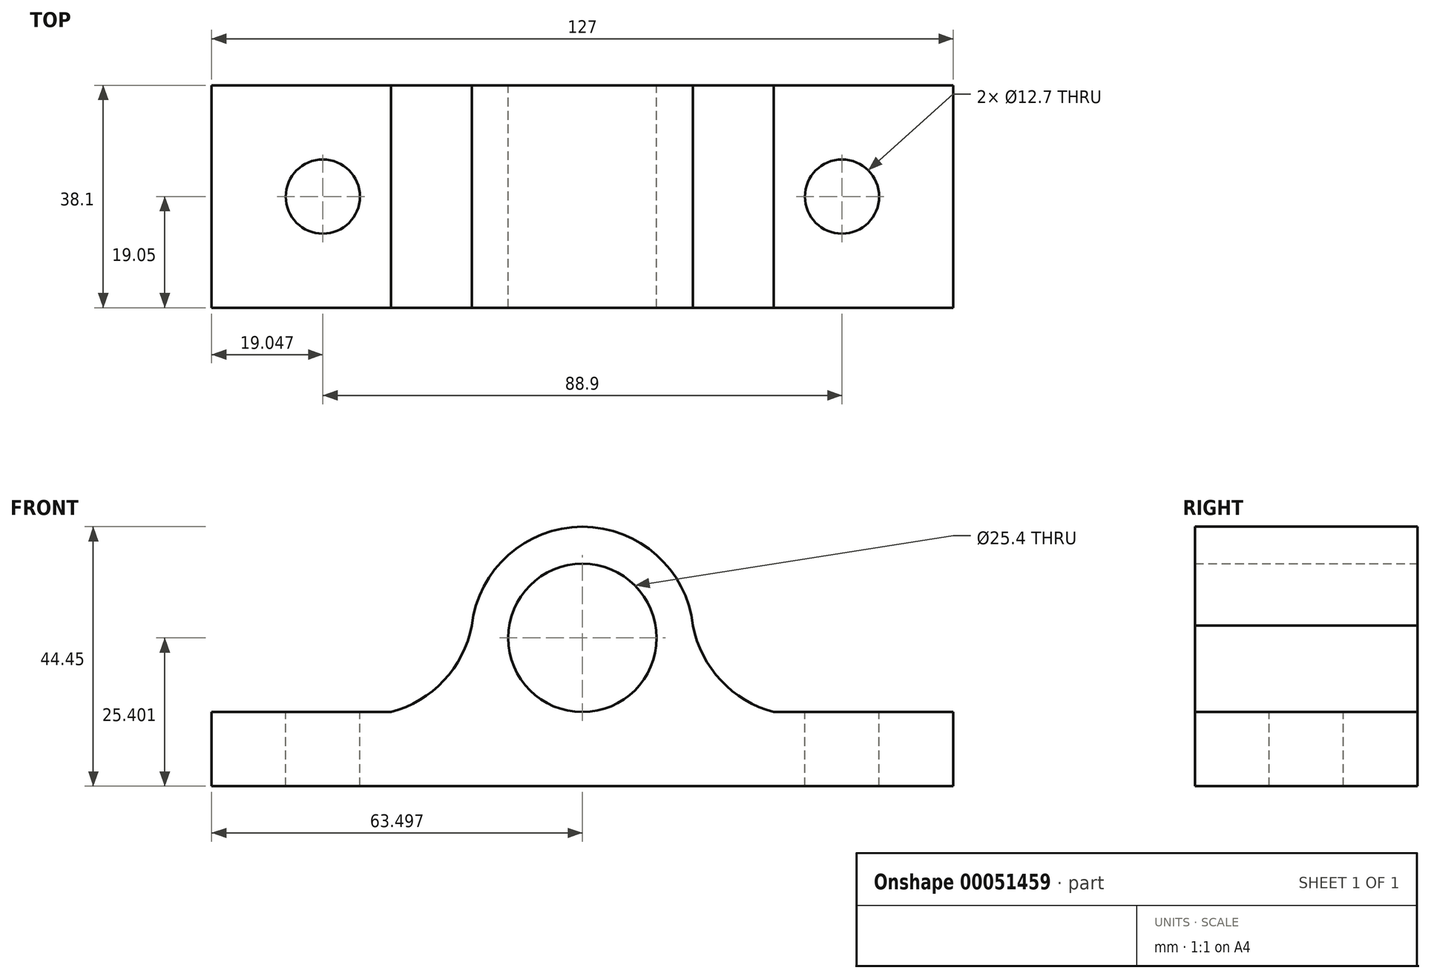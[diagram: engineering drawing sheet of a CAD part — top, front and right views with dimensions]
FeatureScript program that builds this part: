
annotation { "Feature Type Name" : "Feature", "Feature Type Description" : "" }
export const myFeature = defineFeature(function(context is Context, id is Id, definition is map)
    precondition{}
    {
        {
            var Q0;
            Q0=qCreatedBy(makeId("Front.planeOp"),FACE);
            var sketch = newSketch(context, id + "F0", { "sketchPlane" : qUnion([Q0])});
            skLineSegment(sketch, "E0.rect.bottom", {"start": v(23.97, -10) * mm, "end": v(-103.03, -10) * mm});
            skLineSegment(sketch, "E0.rect.top", {"start": v(23.97, 2.7) * mm, "end": v(-6.75, 2.7) * mm});
            skLineSegment(sketch, "E0.rect.left", {"start": v(23.97, -10) * mm, "end": v(23.97, 2.7) * mm});
            skLineSegment(sketch, "E0.rect.right", {"start": v(-103.03, -10) * mm, "end": v(-103.03, 2.7) * mm});
            skPoint(sketch, "E0.rect.middle", {"position": v(-39.53, -3.65) * mm});
            skLineSegment(sketch, "E1.0", {"start": v(23.97, 15.4) * mm, "end": v(-103.03, 15.4) * mm, "construction": true});
            skCircle(sketch, "E2", {"center": v(-39.53, 15.4) * mm, "radius": 12.7 * mm});
            skArc(sketch, "E3", {"start": v(-20.48, 15.4) * mm, "mid": v(-39.53, 34.45) * mm, "end": v(-58.58, 15.4) * mm});
            skLineSegment(sketch, "E4.trimOffspring", {"start": v(-72.32, 2.7) * mm, "end": v(-103.03, 2.7) * mm});
            skArc(sketch, "E5", {"start": v(-72.32, 2.7) * mm, "mid": v(-62.74, 8.68) * mm, "end": v(-58.23, 19.03) * mm});
            skLineSegment(sketch, "E6", {"start": v(-39.53, -3.65) * mm, "end": v(-39.53, 59.53) * mm, "construction": true});
            skArc(sketch, "E7.MirrorCS", {"start": v(-6.75, 2.7) * mm, "mid": v(-16.32, 8.68) * mm, "end": v(-20.83, 19.03) * mm});
            skArc(sketch, "E8.MirrorCS", {"start": v(-58.58, 15.4) * mm, "mid": v(-39.53, 34.45) * mm, "end": v(-20.48, 15.4) * mm});
            skSolve(sketch);
        }
        {
            var Q0;
            Q0 = qSketchRegion(id + "F0", true);
            extrude(context, id + "F1", {"entities" : qUnion([Q0]), "depth" : 38.1 * mm});
        }
        {
            var Q0;
            Q0=makeQuery(id+"F1.opExtrude","SWEPT_FACE",FACE,{"disambiguationData":[OSD([sQuery(id+"F0.wireOp",EDGE,"E4.trimOffspring")])]});
            var sketch = newSketch(context, id + "F2", { "sketchPlane" : qUnion([Q0])});
            skLineSegment(sketch, "E9.0", {"start": v(-83.98, -38.1) * mm, "end": v(-83.98, 0) * mm, "construction": true});
            skLineSegment(sketch, "E10.0", {"start": v(4.92, -38.1) * mm, "end": v(4.92, 0) * mm, "construction": true});
            skCircle(sketch, "E11", {"center": v(-83.98, -19.05) * mm, "radius": 6.35 * mm});
            skCircle(sketch, "E12", {"center": v(4.92, -19.05) * mm, "radius": 6.35 * mm});
            skSolve(sketch);
        }
        {
            var Q0;
            Q0 = qSketchRegion(id + "F2", true);
            extrude(context, id + "F3", {"entities" : qUnion([Q0]), "operationType" : NewBodyOperationType.REMOVE, "oppositeDirection" : true, "depth" : 25.4 * mm});
        }
    });
